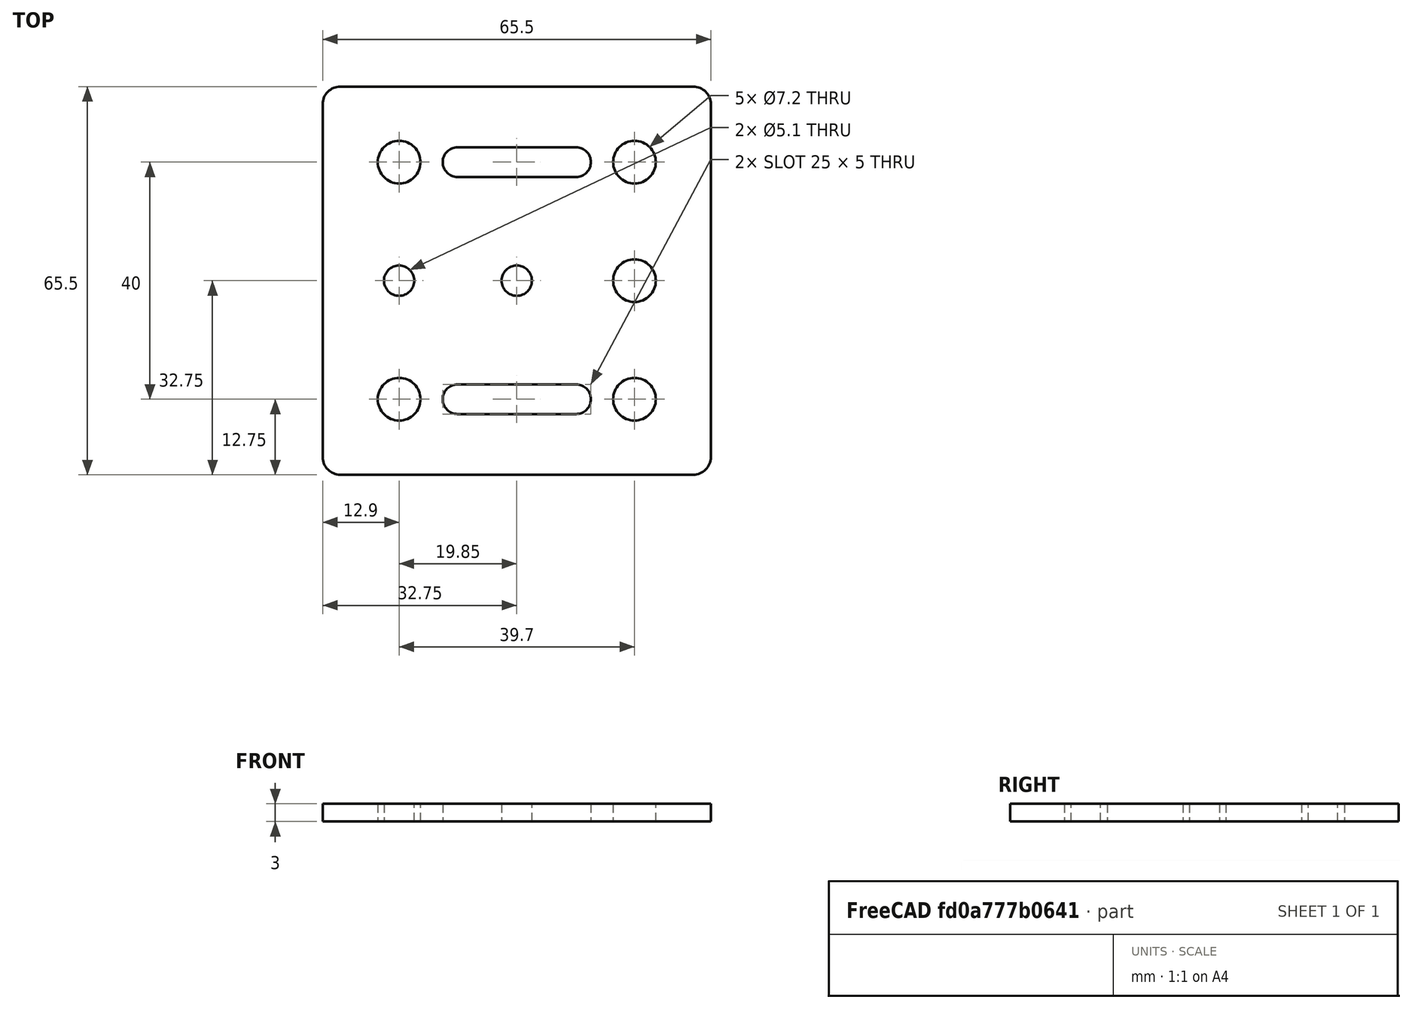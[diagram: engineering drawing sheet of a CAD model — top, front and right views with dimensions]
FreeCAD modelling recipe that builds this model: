
FCSTD DOCUMENT  (FreeCAD 0.20R29177 +426 (Git))
Label: GantryBracket
License: All rights reserved
LicenseURL: http://en.wikipedia.org/wiki/All_rights_reserved
objects: PartDesign::CoordinateSystem×5, App::DocumentObjectGroup×3, App::FeaturePython×1, Sketcher::SketchObject×1, PartDesign::Pad×1, PartDesign::Body×1, App::Part×1
note: 9 computed .brp shape members not serialized (recipe doc carries the construction recipe); baked Part::Feature solids carry a one-line shape summary decoded from their .brp

FEATURE [App::DocumentObjectGroup] Parts
FEATURE [PartDesign::CoordinateSystem] LCS_Origin
  AttacherType = Attacher::AttachEngine3D
  MapMode = 2
  Support = -> [X_Axis]
FEATURE [App::FeaturePython] Variables  # WARN: FeaturePython — macro-defined, semantics opaque (R4)
  Type = App::PropertyContainer
FEATURE [App::DocumentObjectGroup] Constraints
FEATURE [App::DocumentObjectGroup] Configurations
FEATURE [Sketcher::SketchObject] Sketch
  FullyConstrained = true
  MapMode = 5
  Support = -> [XY_Plane001]
  sketch-geometry (29):
    g0: ArcOfCircle CenterX=-29.75 CenterY=29.75 CenterZ=0 NormalX=0 NormalY=0 NormalZ=1 AngleXU=0 Radius=3 StartAngle=1.5708 EndAngle=3.14159
    g1: LineSegment StartX=-29.75 StartY=32.75 StartZ=0 EndX=29.75 EndY=32.75 EndZ=0
    g2: ArcOfCircle CenterX=29.75 CenterY=29.75 CenterZ=0 NormalX=0 NormalY=0 NormalZ=1 AngleXU=0 Radius=3 StartAngle=5e-16 EndAngle=1.5708
    g3: LineSegment StartX=32.75 StartY=29.75 StartZ=0 EndX=32.75 EndY=-29.75 EndZ=0
    g4: ArcOfCircle CenterX=29.75 CenterY=-29.75 CenterZ=0 NormalX=0 NormalY=0 NormalZ=1 AngleXU=0 Radius=3 StartAngle=4.71239 EndAngle=6.28319
    g5: LineSegment StartX=29.75 StartY=-32.75 StartZ=0 EndX=-29.75 EndY=-32.75 EndZ=0
    g6: ArcOfCircle CenterX=-29.75 CenterY=-29.75 CenterZ=0 NormalX=0 NormalY=0 NormalZ=1 AngleXU=0 Radius=3 StartAngle=3.14159 EndAngle=4.71239
    g7: LineSegment StartX=-32.75 StartY=-29.75 StartZ=0 EndX=-32.75 EndY=29.75 EndZ=0
    g8: GeomPoint X=-32.75 Y=32.75 Z=0
    g9: GeomPoint X=32.75 Y=-32.75 Z=0
    g10: Circle CenterX=0 CenterY=0 CenterZ=0 NormalX=0 NormalY=0 NormalZ=1 AngleXU=0 Radius=2.55
    g11: Circle CenterX=-19.85 CenterY=-20 CenterZ=0 NormalX=0 NormalY=0 NormalZ=1 AngleXU=0 Radius=3.6
    g12: Circle CenterX=19.85 CenterY=-20 CenterZ=0 NormalX=0 NormalY=0 NormalZ=1 AngleXU=0 Radius=3.6
    g13: Circle CenterX=19.85 CenterY=20 CenterZ=0 NormalX=0 NormalY=0 NormalZ=1 AngleXU=0 Radius=3.6
    g14: Circle CenterX=-19.85 CenterY=20 CenterZ=0 NormalX=0 NormalY=0 NormalZ=1 AngleXU=0 Radius=3.6
    g15: LineSegment StartX=-19.85 StartY=20 StartZ=0 EndX=19.85 EndY=20 EndZ=0
    g16: LineSegment StartX=19.85 StartY=20 StartZ=0 EndX=19.85 EndY=-20 EndZ=0
    g17: ArcOfCircle CenterX=-10 CenterY=-20 CenterZ=0 NormalX=0 NormalY=0 NormalZ=1 AngleXU=0 Radius=2.5 StartAngle=1.5708 EndAngle=4.71239
    g18: ArcOfCircle CenterX=10 CenterY=-20 CenterZ=0 NormalX=0 NormalY=0 NormalZ=1 AngleXU=0 Radius=2.5 StartAngle=4.71239 EndAngle=7.85398
    g19: LineSegment StartX=-10 StartY=-22.5 StartZ=0 EndX=10 EndY=-22.5 EndZ=0
    g20: LineSegment StartX=10 StartY=-17.5 StartZ=0 EndX=-10 EndY=-17.5 EndZ=0
    g21: ArcOfCircle CenterX=-10 CenterY=20 CenterZ=0 NormalX=0 NormalY=0 NormalZ=1 AngleXU=0 Radius=2.5 StartAngle=1.5708 EndAngle=4.71239
    g22: ArcOfCircle CenterX=10 CenterY=20 CenterZ=0 NormalX=0 NormalY=0 NormalZ=1 AngleXU=0 Radius=2.5 StartAngle=4.71239 EndAngle=7.85398
    g23: LineSegment StartX=-10 StartY=17.5 StartZ=0 EndX=10 EndY=17.5 EndZ=0
    g24: LineSegment StartX=10 StartY=22.5 StartZ=0 EndX=-10 EndY=22.5 EndZ=0
    g25: LineSegment StartX=10 StartY=17.5 StartZ=0 EndX=10 EndY=-17.5 EndZ=0
    g26: LineSegment StartX=-19.85 StartY=20 StartZ=0 EndX=-19.85 EndY=0 EndZ=0
    g27: Circle CenterX=-19.85 CenterY=0 CenterZ=0 NormalX=0 NormalY=0 NormalZ=1 AngleXU=0 Radius=2.55
    g28: Circle CenterX=19.85 CenterY=0 CenterZ=0 NormalX=0 NormalY=0 NormalZ=1 AngleXU=0 Radius=3.6
  constraints (69):
    c: Tangent(g0,g1) = 1.5708
    c: Tangent(g1,g2) = 1.5708
    c: Tangent(g2,g3) = 1.5708
    c: Tangent(g3,g4) = 1.5708
    c: Tangent(g4,g5) = 1.5708
    c: Tangent(g5,g6) = 1.5708
    c: Tangent(g6,g7) = 1.5708
    c: Tangent(g7,g0) = 1.5708
    c: Horizontal(g1)
    c: Horizontal(g5)
    c: Vertical(g3)
    c: Vertical(g7)
    c: Equal(g0,g2)
    c: Equal(g2,g4)
    c: Equal(g4,g6)
    c: PointOnObject(g8,g1)
    c: PointOnObject(g8,g7)
    c: PointOnObject(g9,g3)
    c: PointOnObject(g9,g5)
    c: Symmetric(g2,g6,g-1)
    c: DistanceY(g4,g1) = 65.5
    c: Equal(g1,g3)
    c: Radius(g2) = 3
    c: Coincident(g10,g-1)
    c: Equal(g11,g12)
    c: Equal(g12,g13)
    c: Equal(g13,g14)
    c: Coincident(g15,g14)
    c: Coincident(g15,g13)
    c: Coincident(g16,g13)
    c: Coincident(g16,g12)
    c: Vertical(g16)
    c: Horizontal(g15)
    c: Symmetric(g13,g11,g10)
    c: Symmetric(g12,g14,g10)
    c: DistanceY(g14,g0) = 12.75
    c: DistanceX(g0,g14) = 12.9
    c: Diameter(g13) = 7.2
    c: Diameter(g10) = 5.1
    c: Tangent(g17,g19) = -1.5708
    c: Tangent(g19,g18) = -1.5708
    c: Tangent(g18,g20) = -1.5708
    c: Tangent(g20,g17) = -1.5708
    c: Equal(g17,g18)
    c: Horizontal(g19)
    c: Tangent(g21,g23) = -1.5708
    c: Tangent(g23,g22) = -1.5708
    c: Tangent(g22,g24) = -1.5708
    c: Tangent(g24,g21) = -1.5708
    c: Equal(g21,g22)
    c: Equal(g22,g18)
    c: Equal(g20,g23)
    c: Diameter(g22) = 5
    c: Symmetric(g18,g21,g10)
    c: Horizontal(g23)
    c: PointOnObject(g22,g15)
    c: Coincident(g25,g22)
    c: Coincident(g25,g18)
    c: Vertical(g25)
    c: DistanceX(g24,g24) = 20
    c: Coincident(g26,g14)
    c: PointOnObject(g26,g-1)
    c: Vertical(g26)
    c: Coincident(g27,g26)
    c: PointOnObject(g28,g16)
    c: PointOnObject(g28,g-1)
    c: Equal(g28,g13)
    c: Equal(g27,g10)
    c: DistanceX(g27,g28) = 39.7  'HoleSpacing'
FEATURE [PartDesign::Pad] Pad
  Direction = (0,0,1)
  Length = 3
  Length2 = 10
  Profile = -> Sketch
  ReferenceAxis = -> Sketch [N_Axis]
  Type = 0
FEATURE [PartDesign::Body] Body
  Group = -> [Sketch,Pad]
  Origin = -> Origin001
  Tip = -> Pad
FEATURE [PartDesign::CoordinateSystem] LCS_wheel1
  AttacherType = Attacher::AttachEngine3D
  MapMode = 11
  Placement = pos=(-19.85,20,3) rot=(0,0,1;1.5708rad)
  Support = -> [Pad]
FEATURE [PartDesign::CoordinateSystem] LCS_wheel2
  AttacherType = Attacher::AttachEngine3D
  MapMode = 11
  Placement = pos=(19.85,20,3) rot=(0,0,1;1.5708rad)
  Support = -> [Pad]
FEATURE [PartDesign::CoordinateSystem] LCS_wheel3
  AttacherType = Attacher::AttachEngine3D
  MapMode = 11
  Placement = pos=(-19.85,-20,3) rot=(0,0,1;1.5708rad)
  Support = -> [Pad]
FEATURE [PartDesign::CoordinateSystem] LCS_wheel4
  AttacherType = Attacher::AttachEngine3D
  MapMode = 11
  Placement = pos=(19.85,-20,3) rot=(0,0,1;1.5708rad)
  Support = -> [Pad]
FEATURE [App::Part] Assembly
  AssemblyType = Part::Link
  Group = -> [LCS_Origin,Variables,Constraints,Configurations,Body,LCS_wheel1,LCS_wheel2,LCS_wheel3,LCS_wheel4]
  Origin = -> Origin
  Type = Assembly
